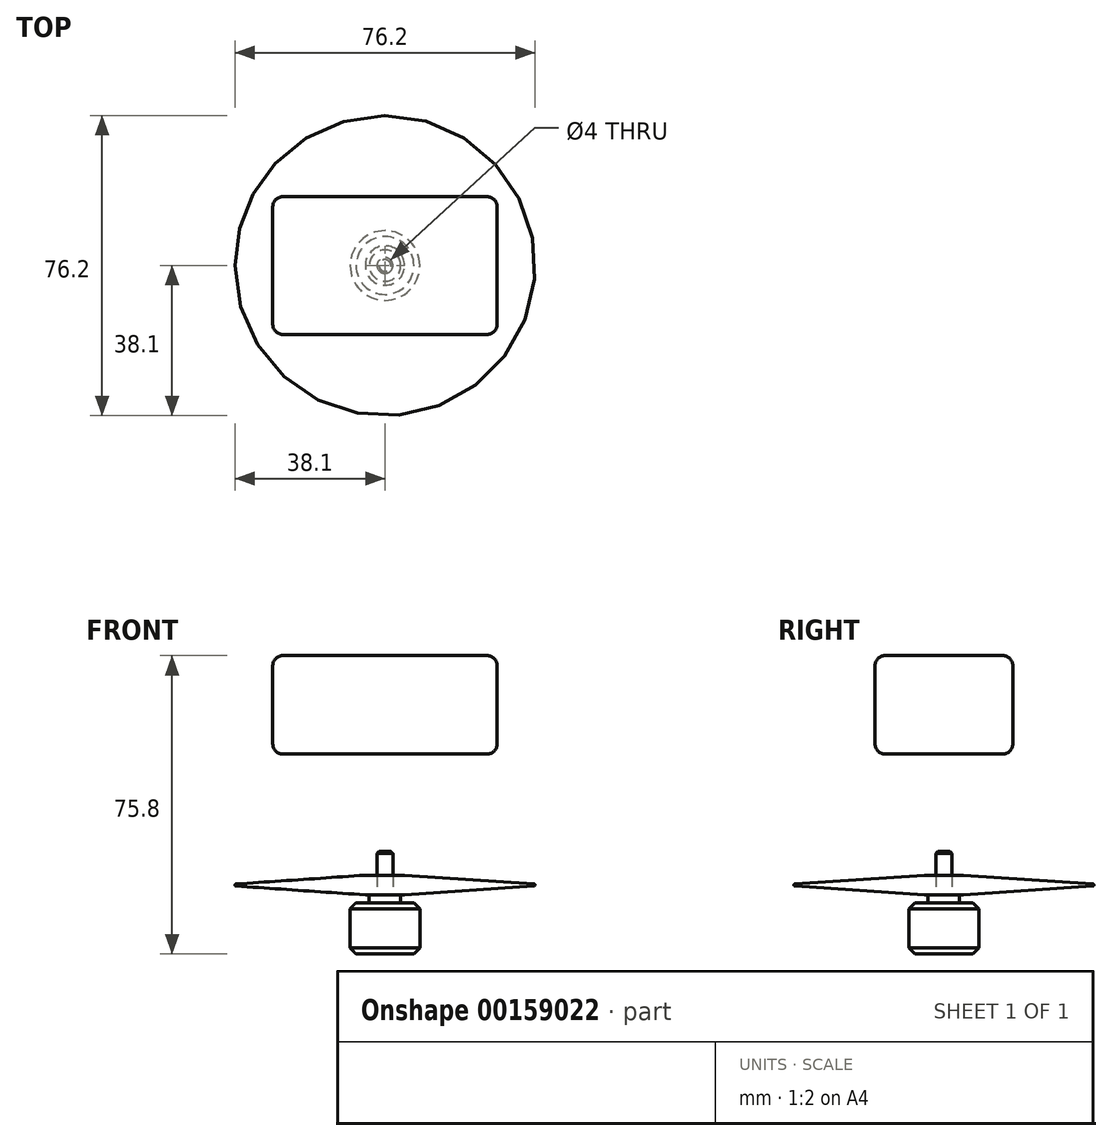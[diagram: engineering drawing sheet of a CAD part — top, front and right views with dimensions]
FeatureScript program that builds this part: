
annotation { "Feature Type Name" : "Feature", "Feature Type Description" : "" }
export const myFeature = defineFeature(function(context is Context, id is Id, definition is map)
    precondition{}
    {
        {
            var Q0;
            Q0=qCreatedBy(makeId("Front.planeOp"),FACE);
            var sketch = newSketch(context, id + "F0", { "sketchPlane" : qUnion([Q0])});
            skLineSegment(sketch, "E0", {"start": v(0, 0) * mm, "end": v(7.35, 0) * mm});
            skLineSegment(sketch, "E1", {"start": v(7.35, 0) * mm, "end": v(8.85, 1.5) * mm});
            skLineSegment(sketch, "E2", {"start": v(8.85, 1.5) * mm, "end": v(8.85, 11.5) * mm});
            skLineSegment(sketch, "E3", {"start": v(8.85, 11.5) * mm, "end": v(7.35, 13) * mm});
            skLineSegment(sketch, "E4", {"start": v(7.35, 13) * mm, "end": v(4, 13) * mm});
            skLineSegment(sketch, "E5", {"start": v(4, 13) * mm, "end": v(4, 15) * mm});
            skLineSegment(sketch, "E6", {"start": v(4, 15) * mm, "end": v(2, 15) * mm});
            skLineSegment(sketch, "E7", {"start": v(2, 15) * mm, "end": v(2, 26) * mm});
            skLineSegment(sketch, "E8", {"start": v(2, 26) * mm, "end": v(0, 26) * mm});
            skLineSegment(sketch, "E9", {"start": v(0, 26) * mm, "end": v(0, 0) * mm});
            skLineSegment(sketch, "E10", {"start": v(0, -9.1) * mm, "end": v(0, 30.9) * mm, "construction": true});
            skSolve(sketch);
        }
        {
            var Q0;
            Q0 = qSketchRegion(id + "F0", true);
            var Q1;
            Q1=sQuery(id+"F0.wireOp",EDGE,"E10");
            revolve(context, id + "F1", {"entities" : qUnion([Q0]), "axis" : qUnion([Q1]), "revolveType" : RevolveType.FULL});
        }
        {
            var Q0;
            Q0=makeQuery(id+"F1.opRevolve","SWEPT_EDGE",EDGE,{"disambiguationData":[OSD([sQuery(id+"F0.wireOp",EDGE,"E7"),sQuery(id+"F0.wireOp",EDGE,"E8")])]});
            chamfer(context, id + "F2", {"entities" : qUnion([Q0]), "width" : .5 * mm, "tangentPropagation" : true});
        }
        {
            var Q0;
            Q0=qCreatedBy(makeId("Front.planeOp"),FACE);
            var sketch = newSketch(context, id + "F3", { "sketchPlane" : qUnion([Q0])});
            skLineSegment(sketch, "E11", {"start": v(2, 20) * mm, "end": v(2, 15) * mm});
            skLineSegment(sketch, "E12", {"start": v(2, 15) * mm, "end": v(5, 15) * mm});
            skLineSegment(sketch, "E13", {"start": v(5, 15) * mm, "end": v(37.86, 17.25) * mm});
            skLineSegment(sketch, "E14", {"start": v(37.86, 17.75) * mm, "end": v(5, 20) * mm});
            skLineSegment(sketch, "E15", {"start": v(5, 20) * mm, "end": v(2, 20) * mm});
            skLineSegment(sketch, "E16", {"start": v(0, 0) * mm, "end": v(0, 33.05) * mm, "construction": true});
            skPoint(sketch, "E17.visualSharp", {"position": v(41.57, 17.5) * mm});
            skArc(sketch, "E17.filletArc", {"start": v(37.86, 17.25) * mm, "mid": v(38.1, 17.5) * mm, "end": v(37.86, 17.75) * mm});
            skPoint(sketch, "E18", {"position": v(38.1, 17.5) * mm});
            skPoint(sketch, "E18.positionSnap0", {"position": v(38.1, 17.5) * mm});
            skPoint(sketch, "E19", {"position": v(2, 17.5) * mm});
            skSolve(sketch);
        }
        {
            var Q0;
            Q0 = qSketchRegion(id + "F3", true);
            var Q1;
            Q1=sQuery(id+"F3.wireOp",EDGE,"E16");
            revolve(context, id + "F4", {"entities" : qUnion([Q0]), "axis" : qUnion([Q1]), "revolveType" : RevolveType.FULL});
        }
        {
            var Q0;
            Q0=qCreatedBy(makeId("Top.planeOp"),FACE);
            cPlane(context, id + "F5", {"entities" : qUnion([Q0]), "cplaneType" : CPlaneType.OFFSET, "offset" : 50.8 * mm, "width" : 152.4 * mm, "height" : 152.4 * mm});
        }
        {
            var Q0;
            Q0=qCreatedBy(id+"F5.planeOp",FACE);
            var sketch = newSketch(context, id + "F6", { "sketchPlane" : qUnion([Q0])});
            skLineSegment(sketch, "E20.bottom", {"start": v(28.5, -17.5) * mm, "end": v(-28.5, -17.5) * mm});
            skLineSegment(sketch, "E20.top", {"start": v(28.5, 17.5) * mm, "end": v(-28.5, 17.5) * mm});
            skLineSegment(sketch, "E20.left", {"start": v(28.5, -17.5) * mm, "end": v(28.5, 17.5) * mm});
            skLineSegment(sketch, "E20.right", {"start": v(-28.5, -17.5) * mm, "end": v(-28.5, 17.5) * mm});
            skPoint(sketch, "E20.middle", {"position": v(0, 0) * mm});
            skSolve(sketch);
        }
        {
            var Q0;
            Q0 = qSketchRegion(id + "F6", true);
            extrude(context, id + "F7", {"entities" : qUnion([Q0]), "depth" : 25 * mm});
        }
        {
            var Q0;
            Q0=makeQuery(id+"F7.opExtrude","CAP_FACE",FACE,{"disambiguationData":[OSD([sQuery(id+"F6.wireOp",EDGE,"E20.bottom"),sQuery(id+"F6.wireOp",EDGE,"E20.top"),sQuery(id+"F6.wireOp",EDGE,"E20.left"),sQuery(id+"F6.wireOp",EDGE,"E20.right")])],"isStart":false});
            var Q1;
            Q1=makeQuery(id+"F7.opExtrude","CAP_FACE",FACE,{"disambiguationData":[OSD([sQuery(id+"F6.wireOp",EDGE,"E20.bottom"),sQuery(id+"F6.wireOp",EDGE,"E20.top"),sQuery(id+"F6.wireOp",EDGE,"E20.left"),sQuery(id+"F6.wireOp",EDGE,"E20.right")])],"isStart":true});
            var Q2;
            Q2=makeQuery(id+"F7.opExtrude","SWEPT_EDGE",EDGE,{"disambiguationData":[OSD([sQuery(id+"F6.wireOp",EDGE,"E20.bottom"),sQuery(id+"F6.wireOp",EDGE,"E20.left")])]});
            var Q3;
            Q3=makeQuery(id+"F7.opExtrude","SWEPT_EDGE",EDGE,{"disambiguationData":[OSD([sQuery(id+"F6.wireOp",EDGE,"E20.bottom"),sQuery(id+"F6.wireOp",EDGE,"E20.right")])]});
            var Q4;
            Q4=makeQuery(id+"F7.opExtrude","SWEPT_EDGE",EDGE,{"disambiguationData":[OSD([sQuery(id+"F6.wireOp",EDGE,"E20.top"),sQuery(id+"F6.wireOp",EDGE,"E20.right")])]});
            var Q5;
            Q5=makeQuery(id+"F7.opExtrude","SWEPT_EDGE",EDGE,{"disambiguationData":[OSD([sQuery(id+"F6.wireOp",EDGE,"E20.top"),sQuery(id+"F6.wireOp",EDGE,"E20.left")])]});
            fillet(context, id + "F8", {"entities" : qUnion([Q0, Q1, Q2, Q3, Q4, Q5]), "radius" : 2.54 * mm, "tangentPropagation" : true, "allowEdgeOverflow" : false});
        }
    });
